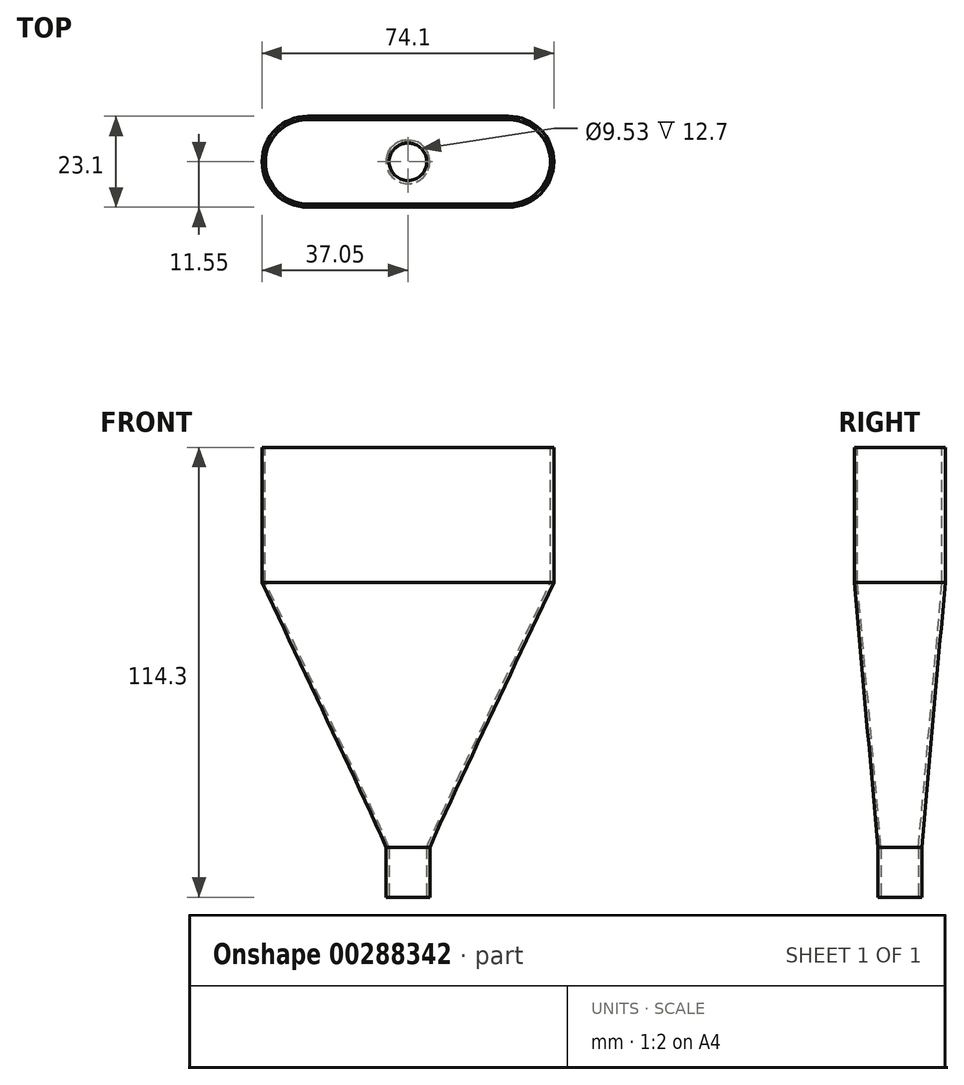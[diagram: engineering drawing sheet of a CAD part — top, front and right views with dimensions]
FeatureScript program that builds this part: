
annotation { "Feature Type Name" : "Feature", "Feature Type Description" : "" }
export const myFeature = defineFeature(function(context is Context, id is Id, definition is map)
    precondition{}
    {
        {
            var Q0;
            Q0=qCreatedBy(makeId("Top.planeOp"),FACE);
            var sketch = newSketch(context, id + "F0", { "sketchPlane" : qUnion([Q0])});
            skLineSegment(sketch, "E0.bottom", {"start": v(25.5, -10.75) * mm, "end": v(-25.5, -10.75) * mm});
            skLineSegment(sketch, "E0.top", {"start": v(25.5, 10.75) * mm, "end": v(-25.5, 10.75) * mm});
            skLineSegment(sketch, "E0.left", {"start": v(25.5, -10.75) * mm, "end": v(25.5, 10.75) * mm, "construction": true});
            skLineSegment(sketch, "E0.right", {"start": v(-25.5, -10.75) * mm, "end": v(-25.5, 10.75) * mm, "construction": true});
            skPoint(sketch, "E0.middle", {"position": v(0, 0) * mm});
            skArc(sketch, "E1", {"start": v(-25.5, 10.75) * mm, "mid": v(-36.25, 0) * mm, "end": v(-25.5, -10.75) * mm});
            skArc(sketch, "E2", {"start": v(-25.5, -10.75) * mm, "mid": v(-14.75, 0) * mm, "end": v(-25.5, 10.75) * mm, "construction": true});
            skArc(sketch, "E3", {"start": v(25.5, 10.75) * mm, "mid": v(14.75, 0) * mm, "end": v(25.5, -10.75) * mm, "construction": true});
            skArc(sketch, "E4", {"start": v(25.5, -10.75) * mm, "mid": v(36.25, 0) * mm, "end": v(25.5, 10.75) * mm});
            skLineSegment(sketch, "E5.0", {"start": v(25.5, 11.55) * mm, "end": v(-25.5, 11.55) * mm});
            skArc(sketch, "E5.1", {"start": v(25.5, -11.55) * mm, "mid": v(37.05, 0) * mm, "end": v(25.5, 11.55) * mm});
            skLineSegment(sketch, "E5.2", {"start": v(25.5, -11.55) * mm, "end": v(-25.5, -11.55) * mm});
            skArc(sketch, "E5.3", {"start": v(-25.5, 11.55) * mm, "mid": v(-37.05, 0) * mm, "end": v(-25.5, -11.55) * mm});
            skPoint(sketch, "E6", {"position": v(-37.05, 0) * mm});
            skPoint(sketch, "E7", {"position": v(37.05, 0) * mm});
            skSolve(sketch);
        }
        {
            var Q0;
            Q0=qCreatedBy(makeId("Front.planeOp"),FACE);
            var sketch = newSketch(context, id + "F1", { "sketchPlane" : qUnion([Q0])});
            skLineSegment(sketch, "E8", {"start": v(0, 0) * mm, "end": v(0, -34.3) * mm, "construction": true});
            skLineSegment(sketch, "E9", {"start": v(0, -34.3) * mm, "end": v(0, -101.6) * mm, "construction": true});
            skLineSegment(sketch, "E10", {"start": v(0, -101.6) * mm, "end": v(0, -114.3) * mm, "construction": true});
            skSolve(sketch);
        }
        {
            var Q0;
            Q0=qCreatedBy(makeId("Top.planeOp"),FACE);
            var Q1;
            Q1=sQuery(id+"F1.wireOp",VERTEX,"E10.end");
            cPlane(context, id + "F2", {"entities" : qUnion([Q0, Q1]), "cplaneType" : CPlaneType.PLANE_POINT, "offset" : 25.4 * mm, "width" : 152.4 * mm, "height" : 152.4 * mm});
        }
        {
            var Q0;
            Q0=qCreatedBy(id+"F2.planeOp",FACE);
            var sketch = newSketch(context, id + "F3", { "sketchPlane" : qUnion([Q0])});
            skCircle(sketch, "E11", {"center": v(0, 0) * mm, "radius": 4.76 * mm});
            skCircle(sketch, "E12.0", {"center": v(0, 0) * mm, "radius": 5.56 * mm});
            skLineSegment(sketch, "E13", {"start": v(5.56, 0) * mm, "end": v(-5.56, 0) * mm, "construction": true});
            skLineSegment(sketch, "E14", {"start": v(0, 5.56) * mm, "end": v(0, -5.56) * mm, "construction": true});
            skLineSegment(sketch, "E15", {"start": v(-0.83, 4.7) * mm, "end": v(-0.97, 5.48) * mm, "construction": true});
            skLineSegment(sketch, "E16.MirrorCS", {"start": v(0.83, 4.7) * mm, "end": v(0.97, 5.48) * mm, "construction": true});
            skLineSegment(sketch, "E17.MirrorCS", {"start": v(0.83, -4.7) * mm, "end": v(0.97, -5.48) * mm, "construction": true});
            skLineSegment(sketch, "E18.MirrorCS", {"start": v(-0.83, -4.7) * mm, "end": v(-0.97, -5.48) * mm, "construction": true});
            skSolve(sketch);
        }
        {
            var Q0;
            Q0=makeQuery(id+"F0.imprint","IMPRINT",FACE,{"disambiguationData":[TD([[makeQuery(id+"F0.imprint","IMPRINT",EDGE,{"derivedFrom":sQuery(id+"F0.wireOp",EDGE,"E0.bottom")}),1.0]])]});
            var Q1;
            Q1=sQuery(id+"F1.wireOp",VERTEX,"E9.start");
            extrude(context, id + "F4", {"entities" : qUnion([Q0]), "endBound" : BoundingType.UP_TO_VERTEX, "oppositeDirection" : true, "endBoundEntityVertex" : qUnion([Q1]), "depth" : 25.4 * mm});
        }
        {
            var Q0;
            Q0=makeQuery(id+"F3.imprint","IMPRINT",FACE,{"disambiguationData":[TD([[makeQuery(id+"F3.imprint","IMPRINT",EDGE,{"derivedFrom":sQuery(id+"F3.wireOp",EDGE,"E11")}),-1.0]])]});
            var Q1;
            Q1=sQuery(id+"F1.wireOp",VERTEX,"E10.start");
            extrude(context, id + "F5", {"entities" : qUnion([Q0]), "operationType" : NewBodyOperationType.ADD, "endBound" : BoundingType.UP_TO_VERTEX, "endBoundEntityVertex" : qUnion([Q1]), "depth" : 25.4 * mm});
        }
        {
            var Q0;
            Q0=sQuery(id+"F1.wireOp",VERTEX,"E9.start");
            var Q1;
            Q1=qCreatedBy(makeId("Top.planeOp"),FACE);
            cPlane(context, id + "F6", {"entities" : qUnion([Q0, Q1]), "cplaneType" : CPlaneType.PLANE_POINT, "offset" : 25.4 * mm, "width" : 152.4 * mm, "height" : 152.4 * mm});
        }
        {
            var Q0;
            Q0=qCreatedBy(id+"F6.planeOp",FACE);
            var sketch = newSketch(context, id + "F7", { "sketchPlane" : qUnion([Q0])});
            skLineSegment(sketch, "E19.0", {"start": v(25.5, -11.55) * mm, "end": v(-25.5, -11.55) * mm});
            skArc(sketch, "E19.1", {"start": v(-25.5, 11.55) * mm, "mid": v(-37.05, 0) * mm, "end": v(-25.5, -11.55) * mm});
            skLineSegment(sketch, "E19.2", {"start": v(25.5, 11.55) * mm, "end": v(-25.5, 11.55) * mm});
            skArc(sketch, "E19.3", {"start": v(25.5, -11.55) * mm, "mid": v(37.05, 0) * mm, "end": v(25.5, 11.55) * mm});
            skSolve(sketch);
        }
        {
            var Q0;
            Q0=qCreatedBy(id+"F6.planeOp",FACE);
            var sketch = newSketch(context, id + "F8", { "sketchPlane" : qUnion([Q0])});
            skLineSegment(sketch, "E20.0", {"start": v(25.5, -10.75) * mm, "end": v(-25.5, -10.75) * mm});
            skArc(sketch, "E20.1", {"start": v(-25.5, 10.75) * mm, "mid": v(-36.25, 0) * mm, "end": v(-25.5, -10.75) * mm});
            skLineSegment(sketch, "E20.2", {"start": v(25.5, 10.75) * mm, "end": v(-25.5, 10.75) * mm});
            skArc(sketch, "E20.3", {"start": v(25.5, -10.75) * mm, "mid": v(36.25, 0) * mm, "end": v(25.5, 10.75) * mm});
            skSolve(sketch);
        }
        {
            var Q0;
            Q0=sQuery(id+"F1.wireOp",VERTEX,"E10.start");
            var Q1;
            Q1=qCreatedBy(id+"F2.planeOp",FACE);
            cPlane(context, id + "F9", {"entities" : qUnion([Q0, Q1]), "cplaneType" : CPlaneType.PLANE_POINT, "offset" : 25.4 * mm, "width" : 152.4 * mm, "height" : 152.4 * mm});
        }
        {
            var Q0;
            Q0=qCreatedBy(id+"F9.planeOp",FACE);
            var sketch = newSketch(context, id + "F10", { "sketchPlane" : qUnion([Q0])});
            skCircle(sketch, "E21.0", {"center": v(0, 0) * mm, "radius": 5.56 * mm});
            skSolve(sketch);
        }
        {
            var Q0;
            Q0=qCreatedBy(id+"F9.planeOp",FACE);
            var sketch = newSketch(context, id + "F11", { "sketchPlane" : qUnion([Q0])});
            skCircle(sketch, "E22.0", {"center": v(0, 0) * mm, "radius": 4.76 * mm});
            skSolve(sketch);
        }
        {
            var Q2;
            Q2=makeQuery(id+"F7.imprint","IMPRINT",FACE,{"disambiguationData":[TD([[makeQuery(id+"F7.imprint","IMPRINT",EDGE,{"derivedFrom":sQuery(id+"F7.wireOp",EDGE,"E19.0")}),-1.0]])]});
            var Q3;
            Q3=makeQuery(id+"F10.imprint","IMPRINT",FACE,{"disambiguationData":[TD([[makeQuery(id+"F10.imprint","IMPRINT",EDGE,{"derivedFrom":sQuery(id+"F10.wireOp",EDGE,"E21.0")}),1.0]])]});
            loft(context, id + "F12", {"operationType" : NewBodyOperationType.ADD, "sheetProfilesArray" : [{ "sheetProfileEntities" : qUnion([Q2]) }, { "sheetProfileEntities" : qUnion([Q3]) }]});
        }
        {
            var Q1;
            Q1=makeQuery(id+"F8.imprint","IMPRINT",FACE,{"disambiguationData":[TD([[makeQuery(id+"F8.imprint","IMPRINT",EDGE,{"derivedFrom":sQuery(id+"F8.wireOp",EDGE,"E20.0")}),-1.0]])]});
            var Q2;
            Q2=makeQuery(id+"F11.imprint","IMPRINT",FACE,{"disambiguationData":[TD([[makeQuery(id+"F11.imprint","IMPRINT",EDGE,{"derivedFrom":sQuery(id+"F11.wireOp",EDGE,"E22.0")}),1.0]])]});
            loft(context, id + "F13", {"operationType" : NewBodyOperationType.REMOVE, "sheetProfilesArray" : [{ "sheetProfileEntities" : qUnion([Q1]) }, { "sheetProfileEntities" : qUnion([Q2]) }]});
        }
    });
